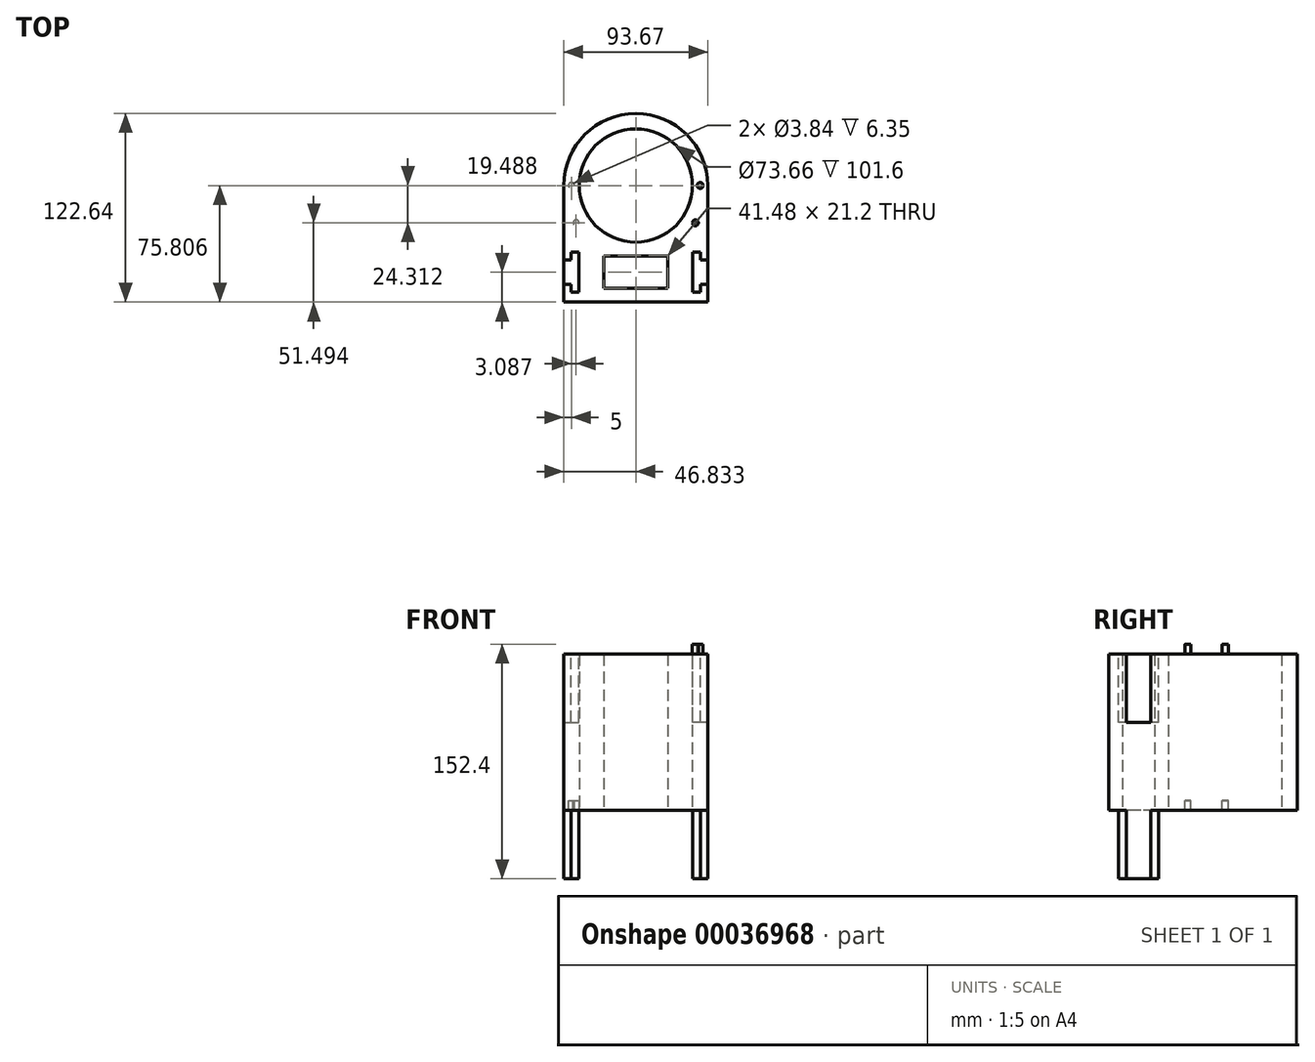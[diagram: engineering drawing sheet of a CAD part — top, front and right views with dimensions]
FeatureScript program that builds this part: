
annotation { "Feature Type Name" : "Feature", "Feature Type Description" : "" }
export const myFeature = defineFeature(function(context is Context, id is Id, definition is map)
    precondition{}
    {
        {
            var Q0;
            Q0=qCreatedBy(makeId("Top.planeOp"),FACE);
            var sketch = newSketch(context, id + "F0", { "sketchPlane" : qUnion([Q0])});
            skCircle(sketch, "E0", {"center": v(14.85, 48.89) * mm, "radius": 36.83 * mm});
            skArc(sketch, "E1", {"start": v(61.69, 48.89) * mm, "mid": v(14.85, 95.72) * mm, "end": v(-31.98, 48.89) * mm});
            skLineSegment(sketch, "E2", {"start": v(-31.98, 48.89) * mm, "end": v(-31.98, -26.92) * mm});
            skLineSegment(sketch, "E3", {"start": v(61.69, 48.89) * mm, "end": v(61.69, -26.92) * mm});
            skLineSegment(sketch, "E4", {"start": v(-31.98, -26.92) * mm, "end": v(61.69, -26.92) * mm});
            skLineSegment(sketch, "E5.rect.bottom", {"start": v(35.6, 3.17) * mm, "end": v(-5.89, 3.17) * mm});
            skLineSegment(sketch, "E5.rect.top", {"start": v(35.6, -18.03) * mm, "end": v(-5.89, -18.03) * mm});
            skLineSegment(sketch, "E5.rect.left", {"start": v(35.6, 3.17) * mm, "end": v(35.6, -18.03) * mm});
            skLineSegment(sketch, "E5.rect.right", {"start": v(-5.89, 3.17) * mm, "end": v(-5.89, -18.03) * mm});
            skPoint(sketch, "E5.rect.middle", {"position": v(14.85, -7.43) * mm});
            skSolve(sketch);
        }
        {
            var Q0;
            Q0=makeQuery(id+"F0.imprint","IMPRINT",FACE,{"disambiguationData":[TD([[makeQuery(id+"F0.imprint","IMPRINT",EDGE,{"derivedFrom":sQuery(id+"F0.wireOp",EDGE,"E0")}),-1.0]])]});
            extrude(context, id + "F1", {"entities" : qUnion([Q0]), "depth" : 101.6 * mm});
        }
        {
            var Q0;
            Q0=qCreatedBy(makeId("Top.planeOp"),FACE);
            var sketch = newSketch(context, id + "F2", { "sketchPlane" : qUnion([Q0])});
            skCircle(sketch, "E6", {"center": v(14.85, 90.72) * mm, "radius": 1.92 * mm});
            skCircle(sketch, "E7", {"center": v(14.85, 48.89) * mm, "radius": 21.92 * mm, "construction": true});
            skLineSegment(sketch, "E8", {"start": v(0, 79.45) * mm, "end": v(13.29, 79.45) * mm, "construction": true});
            skLineSegment(sketch, "E9", {"start": v(13.29, 79.45) * mm, "end": v(26.83, 79.45) * mm, "construction": true});
            skLineSegment(sketch, "E10", {"start": v(14.85, 48.89) * mm, "end": v(14.85, 99.03) * mm, "construction": true});
            skSolve(sketch);
        }
        {
            var Q0;
            Q0=makeQuery(id+"F1.opExtrude","CAP_FACE",FACE,{"disambiguationData":[OSD([sQuery(id+"F0.wireOp",EDGE,"E0"),sQuery(id+"F0.wireOp",EDGE,"E1"),sQuery(id+"F0.wireOp",EDGE,"E2"),sQuery(id+"F0.wireOp",EDGE,"E3"),sQuery(id+"F0.wireOp",EDGE,"E4"),sQuery(id+"F0.wireOp",EDGE,"E5.rect.bottom"),sQuery(id+"F0.wireOp",EDGE,"E5.rect.top"),sQuery(id+"F0.wireOp",EDGE,"E5.rect.left"),sQuery(id+"F0.wireOp",EDGE,"E5.rect.right")])],"isStart":true});
            var sketch = newSketch(context, id + "F3", { "sketchPlane" : qUnion([Q0])});
            skLineSegment(sketch, "E11.MirrorCS", {"start": v(51.88, 20.07) * mm, "end": v(51.88, -5.7) * mm});
            skLineSegment(sketch, "E12.MirrorCS", {"start": v(56.79, -0.63) * mm, "end": v(56.79, -5.7) * mm});
            skLineSegment(sketch, "E13.MirrorCS", {"start": v(61.69, -0.63) * mm, "end": v(61.69, 15.5) * mm});
            skLineSegment(sketch, "E14.MirrorCS", {"start": v(51.88, 20.07) * mm, "end": v(51.88, 20.57) * mm});
            skLineSegment(sketch, "E15.MirrorCS", {"start": v(56.79, 20.07) * mm, "end": v(56.79, 20.57) * mm});
            skLineSegment(sketch, "E16.MirrorCS", {"start": v(56.79, 20.07) * mm, "end": v(56.79, 15.5) * mm});
            skLineSegment(sketch, "E17", {"start": v(56.79, 15.5) * mm, "end": v(61.69, 15.5) * mm});
            skLineSegment(sketch, "E18", {"start": v(56.79, -0.63) * mm, "end": v(61.69, -0.63) * mm});
            skLineSegment(sketch, "E19", {"start": v(56.79, -5.7) * mm, "end": v(51.88, -5.7) * mm});
            skLineSegment(sketch, "E20", {"start": v(51.88, 20.57) * mm, "end": v(56.79, 20.57) * mm});
            skLineSegment(sketch, "E21", {"start": v(14.85, 18.03) * mm, "end": v(14.85, -3.17) * mm, "construction": true});
            skLineSegment(sketch, "E22.MirrorCS", {"start": v(-22.18, 20.07) * mm, "end": v(-22.18, 20.57) * mm});
            skLineSegment(sketch, "E23.MirrorCS", {"start": v(-27.08, 20.07) * mm, "end": v(-27.08, 20.57) * mm});
            skLineSegment(sketch, "E24.MirrorCS", {"start": v(-22.18, 20.07) * mm, "end": v(-22.18, -5.7) * mm});
            skLineSegment(sketch, "E25.MirrorCS", {"start": v(-31.98, -0.63) * mm, "end": v(-31.98, 15.5) * mm});
            skLineSegment(sketch, "E26.MirrorCS", {"start": v(-27.08, 15.5) * mm, "end": v(-31.98, 15.5) * mm});
            skLineSegment(sketch, "E27.MirrorCS", {"start": v(-27.08, -0.63) * mm, "end": v(-31.98, -0.63) * mm});
            skLineSegment(sketch, "E28.MirrorCS", {"start": v(-22.18, 20.57) * mm, "end": v(-27.08, 20.57) * mm});
            skLineSegment(sketch, "E29.MirrorCS", {"start": v(-27.08, -0.63) * mm, "end": v(-27.08, -5.7) * mm});
            skLineSegment(sketch, "E30.MirrorCS", {"start": v(-27.08, -5.7) * mm, "end": v(-22.18, -5.7) * mm});
            skLineSegment(sketch, "E31.MirrorCS", {"start": v(-27.08, 20.07) * mm, "end": v(-27.08, 15.5) * mm});
            skPoint(sketch, "E32.orphan", {"position": v(-27.08, 22.17) * mm});
            skPoint(sketch, "E33.orphan", {"position": v(56.79, 22.17) * mm});
            skSolve(sketch);
        }
        {
            var Q0;
            Q0 = qSketchRegion(id + "F3", true);
            extrude(context, id + "F4", {"entities" : qUnion([Q0]), "operationType" : NewBodyOperationType.ADD, "depth" : 50.8 * mm});
        }
        {
            var Q0;
            Q0=makeQuery(id+"F1.opExtrude","CAP_FACE",FACE,{"disambiguationData":[OSD([sQuery(id+"F0.wireOp",EDGE,"E0"),sQuery(id+"F0.wireOp",EDGE,"E1"),sQuery(id+"F0.wireOp",EDGE,"E2"),sQuery(id+"F0.wireOp",EDGE,"E3"),sQuery(id+"F0.wireOp",EDGE,"E4"),sQuery(id+"F0.wireOp",EDGE,"E5.rect.bottom"),sQuery(id+"F0.wireOp",EDGE,"E5.rect.top"),sQuery(id+"F0.wireOp",EDGE,"E5.rect.left"),sQuery(id+"F0.wireOp",EDGE,"E5.rect.right")])],"isStart":false});
            var sketch = newSketch(context, id + "F5", { "sketchPlane" : qUnion([Q0])});
            skLineSegment(sketch, "E34.bottom", {"start": v(-31.98, -15.5) * mm, "end": v(-27.08, -15.5) * mm});
            skLineSegment(sketch, "E34.top", {"start": v(-31.98, 0.63) * mm, "end": v(-27.08, 0.63) * mm});
            skLineSegment(sketch, "E34.left", {"start": v(-31.98, -15.5) * mm, "end": v(-31.98, 0.63) * mm});
            skLineSegment(sketch, "E34.right", {"start": v(-22.18, -15.5) * mm, "end": v(-22.18, 0.63) * mm});
            skLineSegment(sketch, "E35.bottom", {"start": v(-27.08, 5.7) * mm, "end": v(-22.18, 5.7) * mm});
            skLineSegment(sketch, "E35.top", {"start": v(-27.08, -20.57) * mm, "end": v(-22.18, -20.57) * mm});
            skLineSegment(sketch, "E35.left", {"start": v(-27.08, 5.7) * mm, "end": v(-27.08, 0.63) * mm});
            skLineSegment(sketch, "E35.right", {"start": v(-22.18, 5.7) * mm, "end": v(-22.18, -20.57) * mm});
            skLineSegment(sketch, "E36.trimOffspring", {"start": v(-27.08, -15.5) * mm, "end": v(-27.08, -20.57) * mm});
            skLineSegment(sketch, "E37", {"start": v(14.85, 3.17) * mm, "end": v(14.85, -18.03) * mm, "construction": true});
            skLineSegment(sketch, "E38.MirrorCS", {"start": v(51.88, -15.5) * mm, "end": v(51.88, 0.63) * mm});
            skLineSegment(sketch, "E39.MirrorCS", {"start": v(56.79, 5.7) * mm, "end": v(51.88, 5.7) * mm});
            skLineSegment(sketch, "E40.MirrorCS", {"start": v(61.69, -15.5) * mm, "end": v(61.69, 0.63) * mm});
            skLineSegment(sketch, "E41.MirrorCS", {"start": v(61.69, 0.63) * mm, "end": v(56.79, 0.63) * mm});
            skLineSegment(sketch, "E42.MirrorCS", {"start": v(61.69, -15.5) * mm, "end": v(56.79, -15.5) * mm});
            skLineSegment(sketch, "E43.MirrorCS", {"start": v(56.79, -20.57) * mm, "end": v(51.88, -20.57) * mm});
            skLineSegment(sketch, "E44.MirrorCS", {"start": v(56.79, 5.7) * mm, "end": v(56.79, 0.63) * mm});
            skLineSegment(sketch, "E45.MirrorCS", {"start": v(56.79, -15.5) * mm, "end": v(56.79, -20.57) * mm});
            skLineSegment(sketch, "E46.MirrorCS", {"start": v(51.88, 5.7) * mm, "end": v(51.88, -20.57) * mm});
            skSolve(sketch);
        }
        {
            var Q0;
            Q0 = qSketchRegion(id + "F5", true);
            extrude(context, id + "F6", {"entities" : qUnion([Q0]), "operationType" : NewBodyOperationType.REMOVE, "oppositeDirection" : true, "depth" : 50.8 * mm});
        }
        {
            var Q0;
            Q0=makeQuery(id+"F1.opExtrude","CAP_FACE",FACE,{"disambiguationData":[OSD([sQuery(id+"F0.wireOp",EDGE,"E0"),sQuery(id+"F0.wireOp",EDGE,"E1"),sQuery(id+"F0.wireOp",EDGE,"E2"),sQuery(id+"F0.wireOp",EDGE,"E3"),sQuery(id+"F0.wireOp",EDGE,"E4"),sQuery(id+"F0.wireOp",EDGE,"E5.rect.bottom"),sQuery(id+"F0.wireOp",EDGE,"E5.rect.top"),sQuery(id+"F0.wireOp",EDGE,"E5.rect.left"),sQuery(id+"F0.wireOp",EDGE,"E5.rect.right")])],"isStart":false});
            var sketch = newSketch(context, id + "F7", { "sketchPlane" : qUnion([Q0])});
            skCircle(sketch, "E47", {"center": v(14.85, 90.72) * mm, "radius": 1.92 * mm});
            skLineSegment(sketch, "E48", {"start": v(-31.98, 48.89) * mm, "end": v(61.69, 48.89) * mm, "construction": true});
            skLineSegment(sketch, "E49", {"start": v(-31.98, 48.89) * mm, "end": v(-21.98, 48.89) * mm, "construction": true});
            skLineSegment(sketch, "E50", {"start": v(61.69, 48.89) * mm, "end": v(51.68, 48.89) * mm, "construction": true});
            skCircle(sketch, "E51", {"center": v(-26.98, 48.89) * mm, "radius": 1.92 * mm});
            skCircle(sketch, "E52", {"center": v(-23.9, 24.57) * mm, "radius": 1.92 * mm});
            skCircle(sketch, "E53.MirrorC", {"center": v(56.69, 48.89) * mm, "radius": 1.92 * mm});
            skCircle(sketch, "E54.MirrorC", {"center": v(53.6, 24.57) * mm, "radius": 1.92 * mm});
            skSolve(sketch);
        }
        {
            var Q0;
            Q0=makeQuery(id+"F7.imprint","IMPRINT",FACE,{"disambiguationData":[TD([[makeQuery(id+"F7.imprint","IMPRINT",EDGE,{"derivedFrom":sQuery(id+"F7.wireOp",EDGE,"E51")}),1.0]])]});
            var Q1;
            Q1=makeQuery(id+"F7.imprint","IMPRINT",FACE,{"disambiguationData":[TD([[makeQuery(id+"F7.imprint","IMPRINT",EDGE,{"derivedFrom":sQuery(id+"F7.wireOp",EDGE,"E52")}),1.0]])]});
            var Q2;
            Q2=makeQuery(id+"F7.imprint","IMPRINT",FACE,{"disambiguationData":[TD([[makeQuery(id+"F7.imprint","IMPRINT",EDGE,{"derivedFrom":sQuery(id+"F7.wireOp",EDGE,"E54.MirrorC")}),-1.0]])]});
            var Q3;
            Q3=makeQuery(id+"F7.imprint","IMPRINT",FACE,{"disambiguationData":[TD([[makeQuery(id+"F7.imprint","IMPRINT",EDGE,{"derivedFrom":sQuery(id+"F7.wireOp",EDGE,"E53.MirrorC")}),-1.0]])]});
            var Q4;
            Q4=makeQuery(id+"F7.imprint","IMPRINT",FACE,{"disambiguationData":[TD([[makeQuery(id+"F7.imprint","IMPRINT",EDGE,{"derivedFrom":sQuery(id+"F7.wireOp",EDGE,"E47")}),1.0]])]});
            extrude(context, id + "F8", {"entities" : qUnion([Q0, Q1, Q2, Q3, Q4]), "operationType" : NewBodyOperationType.REMOVE, "oppositeDirection" : true, "depth" : 6.35 * mm});
        }
        {
            var Q0;
            Q0=makeQuery(id+"F1.opExtrude","CAP_FACE",FACE,{"disambiguationData":[OSD([sQuery(id+"F0.wireOp",EDGE,"E0"),sQuery(id+"F0.wireOp",EDGE,"E1"),sQuery(id+"F0.wireOp",EDGE,"E2"),sQuery(id+"F0.wireOp",EDGE,"E3"),sQuery(id+"F0.wireOp",EDGE,"E4"),sQuery(id+"F0.wireOp",EDGE,"E5.rect.bottom"),sQuery(id+"F0.wireOp",EDGE,"E5.rect.top"),sQuery(id+"F0.wireOp",EDGE,"E5.rect.left"),sQuery(id+"F0.wireOp",EDGE,"E5.rect.right")])],"isStart":true});
            var sketch = newSketch(context, id + "F9", { "sketchPlane" : qUnion([Q0])});
            skCircle(sketch, "E55", {"center": v(14.85, -90.72) * mm, "radius": 1.92 * mm});
            skLineSegment(sketch, "E56", {"start": v(61.69, -48.89) * mm, "end": v(51.68, -48.89) * mm, "construction": true});
            skCircle(sketch, "E57", {"center": v(56.69, -48.89) * mm, "radius": 1.92 * mm});
            skCircle(sketch, "E58", {"center": v(53.6, -24.57) * mm, "radius": 1.92 * mm});
            skCircle(sketch, "E59.MirrorC", {"center": v(-23.9, -24.57) * mm, "radius": 1.92 * mm});
            skCircle(sketch, "E60.MirrorC", {"center": v(-26.98, -48.89) * mm, "radius": 1.92 * mm});
            skSolve(sketch);
        }
        {
            var Q0;
            Q0=makeQuery(id+"F9.imprint","IMPRINT",FACE,{"disambiguationData":[TD([[makeQuery(id+"F9.imprint","IMPRINT",EDGE,{"derivedFrom":sQuery(id+"F9.wireOp",EDGE,"E57")}),1.0]])]});
            var Q1;
            Q1=makeQuery(id+"F9.imprint","IMPRINT",FACE,{"disambiguationData":[TD([[makeQuery(id+"F9.imprint","IMPRINT",EDGE,{"derivedFrom":sQuery(id+"F9.wireOp",EDGE,"E55")}),1.0]])]});
            var Q2;
            Q2=makeQuery(id+"F9.imprint","IMPRINT",FACE,{"disambiguationData":[TD([[makeQuery(id+"F9.imprint","IMPRINT",EDGE,{"derivedFrom":sQuery(id+"F9.wireOp",EDGE,"E60.MirrorC")}),-1.0]])]});
            var Q3;
            Q3=makeQuery(id+"F9.imprint","IMPRINT",FACE,{"disambiguationData":[TD([[makeQuery(id+"F9.imprint","IMPRINT",EDGE,{"derivedFrom":sQuery(id+"F9.wireOp",EDGE,"E59.MirrorC")}),-1.0]])]});
            var Q4;
            Q4=makeQuery(id+"F9.imprint","IMPRINT",FACE,{"disambiguationData":[TD([[makeQuery(id+"F9.imprint","IMPRINT",EDGE,{"derivedFrom":sQuery(id+"F9.wireOp",EDGE,"E58")}),1.0]])]});
            extrude(context, id + "F10", {"entities" : qUnion([Q0, Q1, Q2, Q3, Q4]), "operationType" : NewBodyOperationType.ADD, "depth" : 6.35 * mm});
        }
    });
